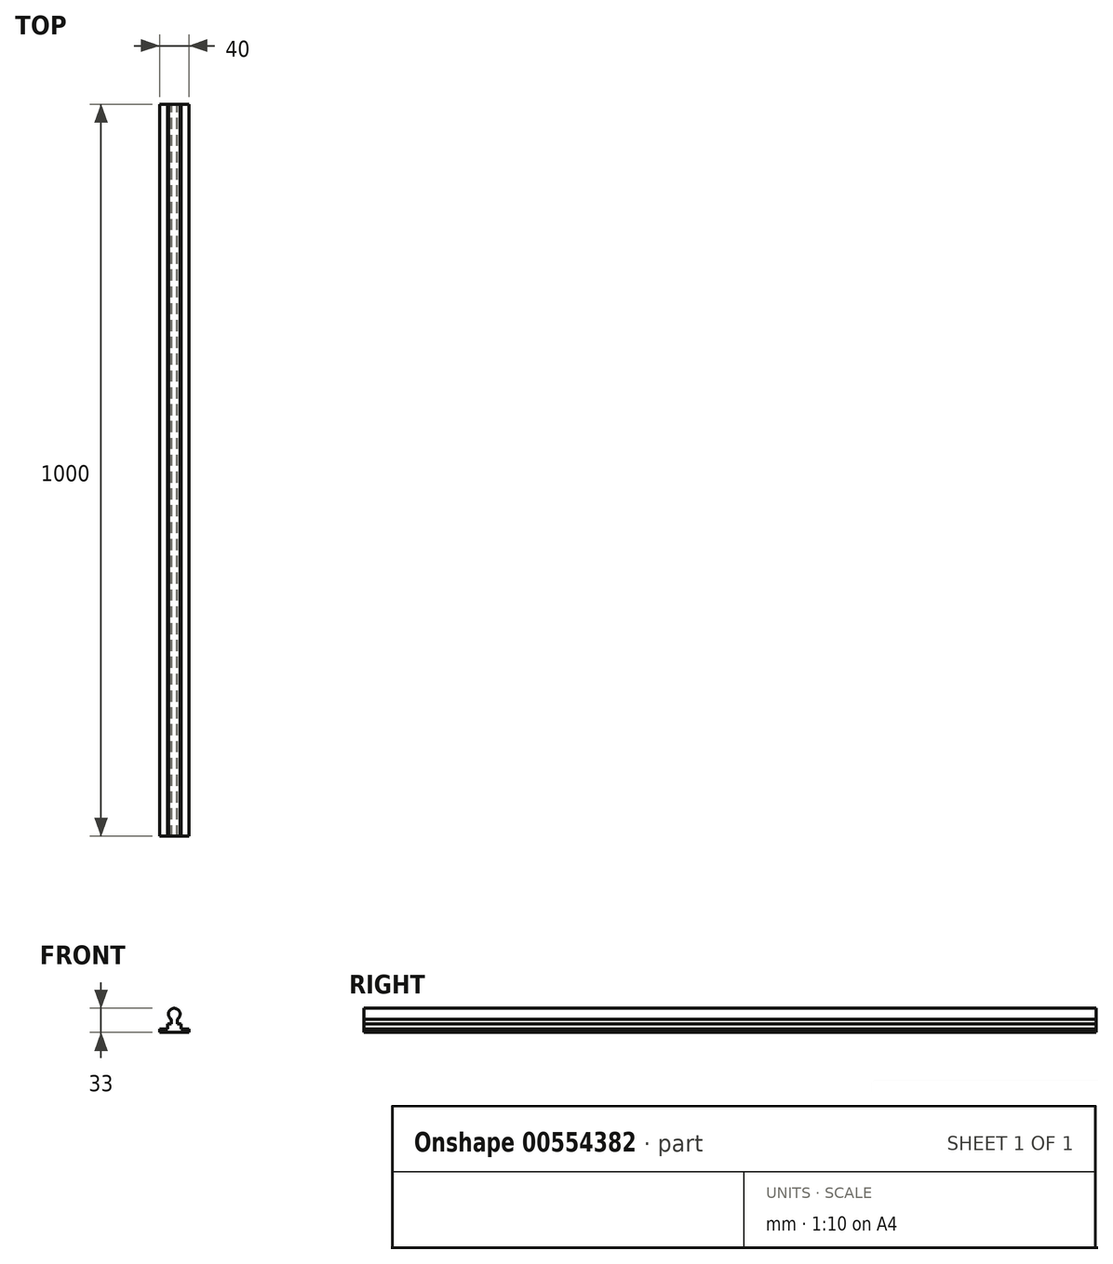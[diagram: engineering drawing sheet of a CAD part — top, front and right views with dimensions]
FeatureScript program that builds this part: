
annotation { "Feature Type Name" : "Feature", "Feature Type Description" : "" }
export const myFeature = defineFeature(function(context is Context, id is Id, definition is map)
    precondition{}
    {
        {
            var Q0;
            Q0=qCreatedBy(makeId("Front.planeOp"),FACE);
            var sketch = newSketch(context, id + "F0", { "sketchPlane" : qUnion([Q0])});
            skLineSegment(sketch, "E0.bottom", {"start": v(-34, -10.6) * mm, "end": v(6, -10.6) * mm});
            skLineSegment(sketch, "E0.top", {"start": v(-34, -5.6) * mm, "end": v(-23.24, -5.6) * mm});
            skLineSegment(sketch, "E0.left", {"start": v(-34, -10.6) * mm, "end": v(-34, -5.6) * mm});
            skLineSegment(sketch, "E0.right", {"start": v(6, -10.6) * mm, "end": v(6, -5.6) * mm});
            skArc(sketch, "E1", {"start": v(-10.5, 7.2) * mm, "mid": v(-14, 22.4) * mm, "end": v(-17.48, 7.2) * mm});
            skLineSegment(sketch, "E2.top", {"start": v(-23.24, 1.05) * mm, "end": v(-18, 1.05) * mm});
            skLineSegment(sketch, "E2.left", {"start": v(-23.24, -5.6) * mm, "end": v(-23.24, 1.05) * mm});
            skLineSegment(sketch, "E2.right", {"start": v(-4.74, -5.6) * mm, "end": v(-4.74, 1.05) * mm});
            skLineSegment(sketch, "E3", {"start": v(-14, 1.05) * mm, "end": v(-14, -5.6) * mm, "construction": true});
            skLineSegment(sketch, "E4.top", {"start": v(-18, 7.2) * mm, "end": v(-17.48, 7.2) * mm});
            skLineSegment(sketch, "E4.left", {"start": v(-18, 1.05) * mm, "end": v(-18, 7.2) * mm});
            skLineSegment(sketch, "E4.right", {"start": v(-10, 1.05) * mm, "end": v(-10, 7.2) * mm});
            skLineSegment(sketch, "E5.bottom", {"start": v(-14, 7.2) * mm, "end": v(-14, 7.2) * mm});
            skLineSegment(sketch, "E5.top", {"start": v(-14, 1.05) * mm, "end": v(-14, 1.05) * mm});
            skLineSegment(sketch, "E5.right", {"start": v(-14, 7.2) * mm, "end": v(-14, 1.05) * mm, "construction": true});
            skLineSegment(sketch, "E6.trimOffspring", {"start": v(-10, 1.05) * mm, "end": v(-4.74, 1.05) * mm});
            skLineSegment(sketch, "E7.trimOffspring", {"start": v(-4.74, -5.6) * mm, "end": v(6, -5.6) * mm});
            skLineSegment(sketch, "E8.trimOffspring", {"start": v(-10.5, 7.2) * mm, "end": v(-10, 7.2) * mm});
            skSolve(sketch);
        }
        {
            var Q0;
            Q0=makeQuery(id+"F0.imprint","IMPRINT",FACE,{"disambiguationData":[TD([[makeQuery(id+"F0.imprint","IMPRINT",EDGE,{"derivedFrom":sQuery(id+"F0.wireOp",EDGE,"E0.bottom")}),1.0]])]});
            extrude(context, id + "F1", {"entities" : qUnion([Q0]), "depth" : 1000 * mm, "offsetDistance" : 25 * mm});
        }
    });
